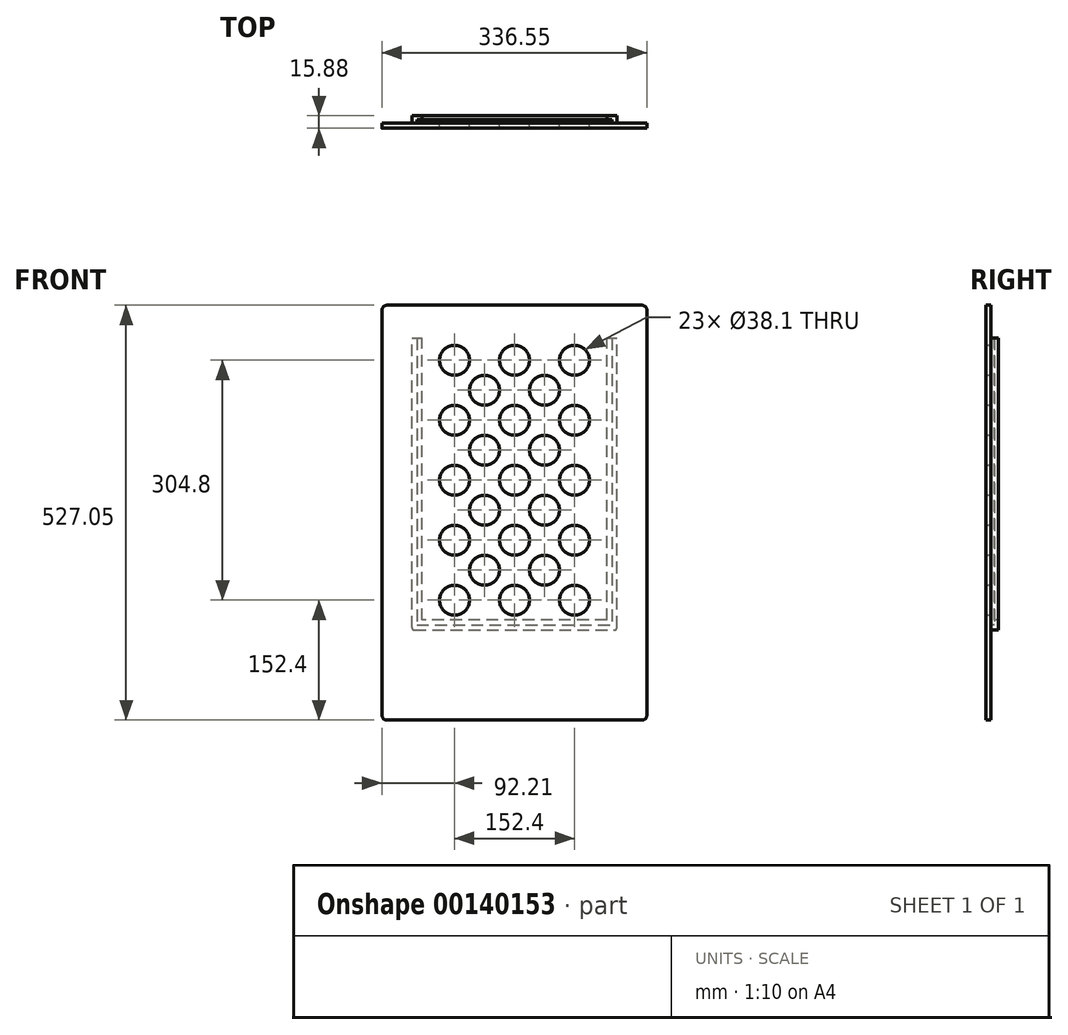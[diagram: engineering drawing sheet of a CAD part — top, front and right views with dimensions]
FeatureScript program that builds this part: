
annotation { "Feature Type Name" : "Feature", "Feature Type Description" : "" }
export const myFeature = defineFeature(function(context is Context, id is Id, definition is map)
    precondition{}
    {
        {
            var Q0;
            Q0=qCreatedBy(makeId("Front.planeOp"),FACE);
            var sketch = newSketch(context, id + "F0", { "sketchPlane" : qUnion([Q0])});
            skCircle(sketch, "E0", {"center": v(-406.4, 596.9) * mm, "radius": 19.05 * mm});
            skCircle(sketch, "E1", {"center": v(-330.2, 596.9) * mm, "radius": 19.05 * mm});
            skCircle(sketch, "E2", {"center": v(-406.4, 520.7) * mm, "radius": 19.05 * mm});
            skCircle(sketch, "E3", {"center": v(-368.3, 558.8) * mm, "radius": 19.05 * mm});
            skCircle(sketch, "E4", {"center": v(-330.2, 520.7) * mm, "radius": 19.05 * mm});
            skCircle(sketch, "E5", {"center": v(-406.4, 444.5) * mm, "radius": 19.05 * mm});
            skCircle(sketch, "E6", {"center": v(-368.3, 482.6) * mm, "radius": 19.05 * mm});
            skCircle(sketch, "E7", {"center": v(-330.2, 444.5) * mm, "radius": 19.05 * mm});
            skCircle(sketch, "E8", {"center": v(-406.4, 368.3) * mm, "radius": 19.05 * mm});
            skCircle(sketch, "E9", {"center": v(-368.3, 406.4) * mm, "radius": 19.05 * mm});
            skCircle(sketch, "E10", {"center": v(-368.3, 330.2) * mm, "radius": 19.05 * mm});
            skCircle(sketch, "E11", {"center": v(-406.4, 292.1) * mm, "radius": 19.05 * mm});
            skCircle(sketch, "E12", {"center": v(-330.2, 292.1) * mm, "radius": 19.05 * mm});
            skCircle(sketch, "E13", {"center": v(-330.2, 368.3) * mm, "radius": 19.05 * mm});
            skCircle(sketch, "E14.MirrorC", {"center": v(-444.5, 406.4) * mm, "radius": 19.05 * mm});
            skCircle(sketch, "E15.MirrorC", {"center": v(-482.6, 596.9) * mm, "radius": 19.05 * mm});
            skCircle(sketch, "E16.MirrorC", {"center": v(-444.5, 482.6) * mm, "radius": 19.05 * mm});
            skCircle(sketch, "E17.MirrorC", {"center": v(-482.6, 368.3) * mm, "radius": 19.05 * mm});
            skCircle(sketch, "E18.MirrorC", {"center": v(-482.6, 520.7) * mm, "radius": 19.05 * mm});
            skCircle(sketch, "E19.MirrorC", {"center": v(-444.5, 558.8) * mm, "radius": 19.05 * mm});
            skCircle(sketch, "E20.MirrorC", {"center": v(-482.6, 292.1) * mm, "radius": 19.05 * mm});
            skCircle(sketch, "E21.MirrorC", {"center": v(-444.5, 330.2) * mm, "radius": 19.05 * mm});
            skCircle(sketch, "E22.MirrorC", {"center": v(-482.6, 444.5) * mm, "radius": 19.05 * mm});
            skLineSegment(sketch, "E23", {"start": v(-574.81, 660.4) * mm, "end": v(-574.81, 146.05) * mm});
            skLineSegment(sketch, "E24", {"start": v(-568.46, 139.7) * mm, "end": v(-244.61, 139.7) * mm});
            skLineSegment(sketch, "E25", {"start": v(-238.26, 660.4) * mm, "end": v(-238.26, 146.05) * mm});
            skLineSegment(sketch, "E26", {"start": v(-568.46, 666.75) * mm, "end": v(-244.61, 666.75) * mm});
            skPoint(sketch, "E27.visualSharp", {"position": v(-574.81, 666.75) * mm});
            skArc(sketch, "E27.filletArc", {"start": v(-568.46, 666.75) * mm, "mid": v(-572.95, 664.9) * mm, "end": v(-574.81, 660.4) * mm});
            skPoint(sketch, "E28.visualSharp", {"position": v(-238.26, 666.75) * mm});
            skArc(sketch, "E28.filletArc", {"start": v(-238.26, 660.4) * mm, "mid": v(-240.12, 664.9) * mm, "end": v(-244.61, 666.75) * mm});
            skPoint(sketch, "E29.visualSharp", {"position": v(-238.26, 139.7) * mm});
            skArc(sketch, "E29.filletArc", {"start": v(-244.61, 139.7) * mm, "mid": v(-240.12, 141.56) * mm, "end": v(-238.26, 146.05) * mm});
            skPoint(sketch, "E30.visualSharp", {"position": v(-574.81, 139.7) * mm});
            skArc(sketch, "E30.filletArc", {"start": v(-574.81, 146.05) * mm, "mid": v(-572.95, 141.56) * mm, "end": v(-568.46, 139.7) * mm});
            skLineSegment(sketch, "E31", {"start": v(-533.54, 254) * mm, "end": v(-279.54, 254) * mm});
            skLineSegment(sketch, "E32", {"start": v(-536.71, 257.17) * mm, "end": v(-536.71, 625.1) * mm});
            skLineSegment(sketch, "E33", {"start": v(-276.36, 257.17) * mm, "end": v(-276.36, 625.1) * mm});
            skLineSegment(sketch, "E34", {"start": v(-530.36, 625.1) * mm, "end": v(-530.36, 260.35) * mm});
            skLineSegment(sketch, "E35", {"start": v(-524.01, 266.7) * mm, "end": v(-524.01, 625.1) * mm});
            skLineSegment(sketch, "E36", {"start": v(-530.36, 260.35) * mm, "end": v(-282.71, 260.35) * mm});
            skLineSegment(sketch, "E37", {"start": v(-282.71, 625.1) * mm, "end": v(-282.71, 260.35) * mm});
            skLineSegment(sketch, "E38.trimOffspring", {"start": v(-289.06, 266.7) * mm, "end": v(-524.01, 266.7) * mm});
            skLineSegment(sketch, "E39.trimOffspring", {"start": v(-289.06, 266.7) * mm, "end": v(-289.06, 625.1) * mm});
            skPoint(sketch, "E40.visualSharp", {"position": v(-536.71, 254) * mm});
            skArc(sketch, "E40.filletArc", {"start": v(-536.71, 257.17) * mm, "mid": v(-535.78, 254.93) * mm, "end": v(-533.54, 254) * mm});
            skPoint(sketch, "E41.visualSharp", {"position": v(-276.36, 254) * mm});
            skArc(sketch, "E41.filletArc", {"start": v(-279.54, 254) * mm, "mid": v(-277.3, 254.93) * mm, "end": v(-276.36, 257.17) * mm});
            skLineSegment(sketch, "E42", {"start": v(-536.71, 625.1) * mm, "end": v(-276.36, 625.1) * mm});
            skSolve(sketch);
        }
        {
            var Q0;
            {var subQ2=sQuery(id+"F0.wireOp",EDGE,"E34");Q0=makeQuery(id+"F0.imprint","IMPRINT",FACE,{"disambiguationData":[TD([[makeQuery(id+"F0.imprint","IMPRINT",EDGE,{"derivedFrom":subQ2}),1.0]])]});}
            extrude(context, id + "F1", {"entities" : qUnion([Q0]), "oppositeDirection" : true, "depth" : 9.52 * mm});
        }
        {
            var Q0;
            {var subQ2=sQuery(id+"F0.wireOp",EDGE,"E34");Q0=makeQuery(id+"F0.imprint","IMPRINT",FACE,{"disambiguationData":[TD([[makeQuery(id+"F0.imprint","IMPRINT",EDGE,{"derivedFrom":subQ2}),1.0]])]});}
            extrude(context, id + "F2", {"entities" : qUnion([Q0]), "operationType" : NewBodyOperationType.REMOVE, "oppositeDirection" : true, "depth" : 4.76 * mm});
        }
        {
            var Q0;
            Q0=makeQuery(id+"F0.imprint","IMPRINT",FACE,{"disambiguationData":[TD([[makeQuery(id+"F0.imprint","IMPRINT",EDGE,{"derivedFrom":sQuery(id+"F0.wireOp",EDGE,"E31")}),1.0]])]});
            extrude(context, id + "F3", {"entities" : qUnion([Q0]), "operationType" : NewBodyOperationType.ADD, "oppositeDirection" : true, "depth" : 9.52 * mm});
        }
        {
            var Q0;
            Q0=makeQuery(id+"F0.imprint","IMPRINT",FACE,{"disambiguationData":[TD([[makeQuery(id+"F0.imprint","IMPRINT",EDGE,{"derivedFrom":sQuery(id+"F0.wireOp",EDGE,"E23")}),1.0]])]});
            var Q1;
            Q1=makeQuery(id+"F0.imprint","IMPRINT",FACE,{"disambiguationData":[TD([[makeQuery(id+"F0.imprint","IMPRINT",EDGE,{"derivedFrom":sQuery(id+"F0.wireOp",EDGE,"E0")}),-1.0]])]});
            var Q2;
            {var subQ2=sQuery(id+"F0.wireOp",EDGE,"E34");Q2=makeQuery(id+"F0.imprint","IMPRINT",FACE,{"disambiguationData":[TD([[makeQuery(id+"F0.imprint","IMPRINT",EDGE,{"derivedFrom":subQ2}),1.0]])]});}
            var Q3;
            Q3=makeQuery(id+"F0.imprint","IMPRINT",FACE,{"disambiguationData":[TD([[makeQuery(id+"F0.imprint","IMPRINT",EDGE,{"derivedFrom":sQuery(id+"F0.wireOp",EDGE,"E31")}),1.0]])]});
            extrude(context, id + "F4", {"entities" : qUnion([Q0, Q1, Q2, Q3]), "operationType" : NewBodyOperationType.ADD, "depth" : 6.35 * mm});
        }
    });
